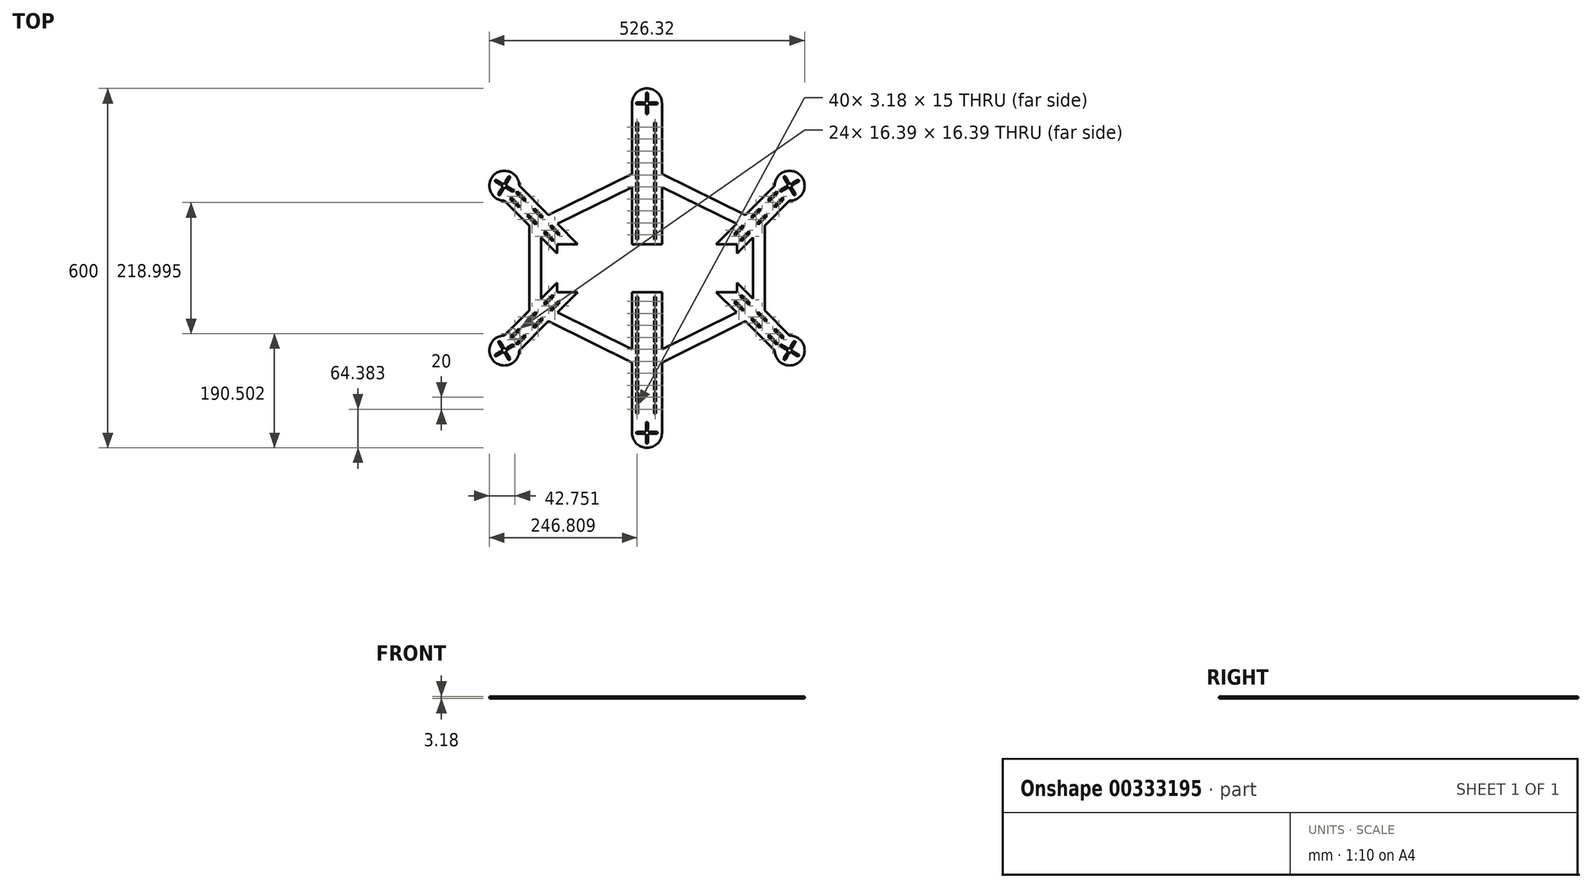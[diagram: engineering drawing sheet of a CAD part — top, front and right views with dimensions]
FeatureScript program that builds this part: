
annotation { "Feature Type Name" : "Feature", "Feature Type Description" : "" }
export const myFeature = defineFeature(function(context is Context, id is Id, definition is map)
    precondition{}
    {
        {
            var Q0;
            Q0=qCreatedBy(makeId("Top.planeOp"),FACE);
            var sketch = newSketch(context, id + "F0", { "sketchPlane" : qUnion([Q0])});
            skPoint(sketch, "E0.middle", {"position": v(0, 0) * mm});
            skCircle(sketch, "E1", {"center": v(0, 275) * mm, "radius": 25 * mm});
            skPoint(sketch, "E1.centerSnap0", {"position": v(0, 301.8) * mm});
            skCircle(sketch, "E2.1.0", {"center": v(-238.16, 137.5) * mm, "radius": 25 * mm});
            skLineSegment(sketch, "E3.bottom", {"start": v(150, -40) * mm, "end": v(-150, -40) * mm});
            skLineSegment(sketch, "E3.top", {"start": v(150, 40) * mm, "end": v(-150, 40) * mm});
            skLineSegment(sketch, "E3.left", {"start": v(150, -40) * mm, "end": v(150, 40) * mm});
            skLineSegment(sketch, "E3.right", {"start": v(-150, -40) * mm, "end": v(-150, 40) * mm});
            skLineSegment(sketch, "E4", {"start": v(-213.16, 137.5) * mm, "end": v(-115.66, 40) * mm});
            skLineSegment(sketch, "E5", {"start": v(-263.16, 137.5) * mm, "end": v(-150, 24.34) * mm});
            skCircle(sketch, "E6.MirrorC", {"center": v(-238.16, -137.5) * mm, "radius": 25 * mm});
            skLineSegment(sketch, "E7", {"start": v(0, 0) * mm, "end": v(0, 86.77) * mm, "construction": true});
            skLineSegment(sketch, "E8.MirrorCS", {"start": v(213.16, 137.5) * mm, "end": v(115.66, 40) * mm});
            skLineSegment(sketch, "E9.MirrorCS", {"start": v(263.16, 137.5) * mm, "end": v(150, 24.34) * mm});
            skCircle(sketch, "E10.MirrorC", {"center": v(238.16, 137.5) * mm, "radius": 25 * mm});
            skCircle(sketch, "E11.MirrorC", {"center": v(238.16, -137.5) * mm, "radius": 25 * mm});
            skLineSegment(sketch, "E12", {"start": v(0, 0) * mm, "end": v(-288.43, 0) * mm, "construction": true});
            skCircle(sketch, "E13.MirrorC", {"center": v(0, -275) * mm, "radius": 25 * mm});
            skLineSegment(sketch, "E14.bottom", {"start": v(-25, 275) * mm, "end": v(25, 275) * mm});
            skLineSegment(sketch, "E14.top", {"start": v(-25, 40) * mm, "end": v(25, 40) * mm});
            skLineSegment(sketch, "E14.left", {"start": v(-25, 275) * mm, "end": v(-25, 40) * mm});
            skLineSegment(sketch, "E14.right", {"start": v(25, 275) * mm, "end": v(25, 40) * mm});
            skLineSegment(sketch, "E15.MirrorCS", {"start": v(-25, -275) * mm, "end": v(-25, -40) * mm});
            skLineSegment(sketch, "E16.MirrorCS", {"start": v(25, -275) * mm, "end": v(25, -40) * mm});
            skLineSegment(sketch, "E17", {"start": v(-25, 157.5) * mm, "end": v(-25, 135.2) * mm});
            skLineSegment(sketch, "E18.MirrorCS", {"start": v(-213.16, -137.5) * mm, "end": v(-115.66, -40) * mm});
            skLineSegment(sketch, "E19.MirrorCS", {"start": v(-263.16, -137.5) * mm, "end": v(-150, -24.34) * mm});
            skLineSegment(sketch, "E20.MirrorCS", {"start": v(263.16, -137.5) * mm, "end": v(150, -24.34) * mm});
            skLineSegment(sketch, "E21.MirrorCS", {"start": v(213.16, -137.5) * mm, "end": v(115.66, -40) * mm});
            skLineSegment(sketch, "E22", {"start": v(-164.4, 88.75) * mm, "end": v(-25, 157.5) * mm});
            skLineSegment(sketch, "E23", {"start": v(-25, 135.2) * mm, "end": v(-149.47, 73.82) * mm});
            skLineSegment(sketch, "E24.MirrorCS", {"start": v(25, 135.2) * mm, "end": v(149.47, 73.82) * mm});
            skLineSegment(sketch, "E25.MirrorCS", {"start": v(164.4, 88.75) * mm, "end": v(25, 157.5) * mm});
            skLineSegment(sketch, "E26.MirrorCS", {"start": v(-25, -135.2) * mm, "end": v(-149.47, -73.82) * mm});
            skLineSegment(sketch, "E27.MirrorCS", {"start": v(-164.4, -88.75) * mm, "end": v(-25, -157.5) * mm});
            skLineSegment(sketch, "E28.MirrorCS", {"start": v(164.4, -88.75) * mm, "end": v(25, -157.5) * mm});
            skLineSegment(sketch, "E29.MirrorCS", {"start": v(25, -135.2) * mm, "end": v(149.47, -73.82) * mm});
            skLineSegment(sketch, "E30", {"start": v(-164.6, -38.94) * mm, "end": v(-188.74, -63.09) * mm});
            skLineSegment(sketch, "E31", {"start": v(-188.74, 63.09) * mm, "end": v(-164.6, 38.94) * mm});
            skLineSegment(sketch, "E32.MirrorCS", {"start": v(188.74, 63.09) * mm, "end": v(164.6, 38.94) * mm});
            skLineSegment(sketch, "E33", {"start": v(-176.67, 51.01) * mm, "end": v(-176.67, -51.01) * mm});
            skLineSegment(sketch, "E34", {"start": v(-196.67, 71.01) * mm, "end": v(-196.67, -71.01) * mm});
            skLineSegment(sketch, "E35.MirrorCS", {"start": v(176.67, 51.01) * mm, "end": v(176.67, -51.01) * mm});
            skLineSegment(sketch, "E36.MirrorCS", {"start": v(196.67, 71.01) * mm, "end": v(196.67, -71.01) * mm});
            skSolve(sketch);
        }
        {
            var Q0;
            Q0=qSketchRegion(id+"F0",true);
            var Q1;
            {var subQ2=sQuery(id+"F0.wireOp",EDGE,"E14.top");Q1=makeQuery(id+"F0.imprint","IMPRINT",FACE,{"disambiguationData":[TD([[makeQuery(id+"F0.imprint","IMPRINT",EDGE,{"derivedFrom":subQ2}),-1.0]])]});}
            extrude(context, id + "F1", {"entities" : qUnion([Q0, Q1]), "depth" : 3.17 * mm});
        }
        {
            var Q0;
            Q0=makeQuery(id+"F1.opExtrude","CAP_FACE",FACE,{"disambiguationData":[OSD([sQuery(id+"F0.wireOp",EDGE,"E1"),sQuery(id+"F0.wireOp",EDGE,"E2.1.0"),sQuery(id+"F0.wireOp",EDGE,"E3.bottom"),sQuery(id+"F0.wireOp",EDGE,"E3.top"),sQuery(id+"F0.wireOp",EDGE,"E3.left"),sQuery(id+"F0.wireOp",EDGE,"E3.right"),sQuery(id+"F0.wireOp",EDGE,"E4"),sQuery(id+"F0.wireOp",EDGE,"E5"),sQuery(id+"F0.wireOp",EDGE,"E6.MirrorC"),sQuery(id+"F0.wireOp",EDGE,"E8.MirrorCS"),sQuery(id+"F0.wireOp",EDGE,"E9.MirrorCS"),sQuery(id+"F0.wireOp",EDGE,"E10.MirrorC"),sQuery(id+"F0.wireOp",EDGE,"E11.MirrorC"),sQuery(id+"F0.wireOp",EDGE,"E13.MirrorC"),sQuery(id+"F0.wireOp",EDGE,"E14.left"),sQuery(id+"F0.wireOp",EDGE,"E14.right"),sQuery(id+"F0.wireOp",EDGE,"E15.MirrorCS"),sQuery(id+"F0.wireOp",EDGE,"E16.MirrorCS"),sQuery(id+"F0.wireOp",EDGE,"E18.MirrorCS"),sQuery(id+"F0.wireOp",EDGE,"E19.MirrorCS"),sQuery(id+"F0.wireOp",EDGE,"E21.MirrorCS"),sQuery(id+"F0.wireOp",EDGE,"E22"),sQuery(id+"F0.wireOp",EDGE,"E23"),sQuery(id+"F0.wireOp",EDGE,"E24.MirrorCS"),sQuery(id+"F0.wireOp",EDGE,"E25.MirrorCS"),sQuery(id+"F0.wireOp",EDGE,"E26.MirrorCS"),sQuery(id+"F0.wireOp",EDGE,"E27.MirrorCS"),sQuery(id+"F0.wireOp",EDGE,"E28.MirrorCS"),sQuery(id+"F0.wireOp",EDGE,"E29.MirrorCS"),sQuery(id+"F0.wireOp",EDGE,"E30"),sQuery(id+"F0.wireOp",EDGE,"E31"),sQuery(id+"F0.wireOp",EDGE,"E32.MirrorCS"),sQuery(id+"F0.wireOp",EDGE,"E20.MirrorCS"),sQuery(id+"F0.wireOp",EDGE,"E33"),sQuery(id+"F0.wireOp",EDGE,"E34"),sQuery(id+"F0.wireOp",EDGE,"E35.MirrorCS"),sQuery(id+"F0.wireOp",EDGE,"E36.MirrorCS")])],"isStart":false});
            var sketch = newSketch(context, id + "F2", { "sketchPlane" : qUnion([Q0])});
            skLineSegment(sketch, "E37.bottom", {"start": v(-17.94, 243.12) * mm, "end": v(-14.76, 243.12) * mm});
            skLineSegment(sketch, "E37.top", {"start": v(-17.94, 228.12) * mm, "end": v(-14.76, 228.12) * mm});
            skLineSegment(sketch, "E37.left", {"start": v(-17.94, 243.12) * mm, "end": v(-17.94, 228.12) * mm});
            skLineSegment(sketch, "E37.right", {"start": v(-14.76, 243.12) * mm, "end": v(-14.76, 228.12) * mm});
            skLineSegment(sketch, "E38.1.0.0", {"start": v(12.06, 243.12) * mm, "end": v(15.24, 243.12) * mm});
            skLineSegment(sketch, "E38.1.0.1", {"start": v(12.06, 243.12) * mm, "end": v(12.06, 228.12) * mm});
            skLineSegment(sketch, "E38.1.0.2", {"start": v(15.24, 243.12) * mm, "end": v(15.24, 228.12) * mm});
            skLineSegment(sketch, "E38.1.0.3", {"start": v(12.06, 228.12) * mm, "end": v(15.24, 228.12) * mm});
            skLineSegment(sketch, "E38.direction1", {"start": v(-17.94, 243.12) * mm, "end": v(12.06, 243.12) * mm, "construction": true});
            skLineSegment(sketch, "E39.0.1.0", {"start": v(-17.94, 223.12) * mm, "end": v(12.06, 223.12) * mm, "construction": true});
            skLineSegment(sketch, "E39.0.1.1", {"start": v(-14.76, 223.12) * mm, "end": v(-14.76, 208.12) * mm});
            skLineSegment(sketch, "E39.0.1.2", {"start": v(-17.94, 223.12) * mm, "end": v(-17.94, 208.12) * mm});
            skLineSegment(sketch, "E39.0.1.3", {"start": v(15.24, 223.12) * mm, "end": v(15.24, 208.12) * mm});
            skLineSegment(sketch, "E39.0.1.4", {"start": v(12.06, 223.12) * mm, "end": v(12.06, 208.12) * mm});
            skLineSegment(sketch, "E39.0.1.5", {"start": v(12.06, 208.12) * mm, "end": v(15.24, 208.12) * mm});
            skLineSegment(sketch, "E39.0.1.6", {"start": v(-17.94, 223.12) * mm, "end": v(-14.76, 223.12) * mm});
            skLineSegment(sketch, "E39.0.1.7", {"start": v(-17.94, 208.12) * mm, "end": v(-14.76, 208.12) * mm});
            skLineSegment(sketch, "E39.0.1.8", {"start": v(12.06, 223.12) * mm, "end": v(15.24, 223.12) * mm});
            skLineSegment(sketch, "E39.0.2.0", {"start": v(-17.94, 203.12) * mm, "end": v(12.06, 203.12) * mm, "construction": true});
            skLineSegment(sketch, "E39.0.2.1", {"start": v(-14.76, 203.12) * mm, "end": v(-14.76, 188.12) * mm});
            skLineSegment(sketch, "E39.0.2.2", {"start": v(-17.94, 203.12) * mm, "end": v(-17.94, 188.12) * mm});
            skLineSegment(sketch, "E39.0.2.3", {"start": v(15.24, 203.12) * mm, "end": v(15.24, 188.12) * mm});
            skLineSegment(sketch, "E39.0.2.4", {"start": v(12.06, 203.12) * mm, "end": v(12.06, 188.12) * mm});
            skLineSegment(sketch, "E39.0.2.5", {"start": v(12.06, 188.12) * mm, "end": v(15.24, 188.12) * mm});
            skLineSegment(sketch, "E39.0.2.6", {"start": v(-17.94, 203.12) * mm, "end": v(-14.76, 203.12) * mm});
            skLineSegment(sketch, "E39.0.2.7", {"start": v(-17.94, 188.12) * mm, "end": v(-14.76, 188.12) * mm});
            skLineSegment(sketch, "E39.0.2.8", {"start": v(12.06, 203.12) * mm, "end": v(15.24, 203.12) * mm});
            skLineSegment(sketch, "E39.0.3.0", {"start": v(-17.94, 183.12) * mm, "end": v(12.06, 183.12) * mm, "construction": true});
            skLineSegment(sketch, "E39.0.3.1", {"start": v(-14.76, 183.12) * mm, "end": v(-14.76, 168.12) * mm});
            skLineSegment(sketch, "E39.0.3.2", {"start": v(-17.94, 183.12) * mm, "end": v(-17.94, 168.12) * mm});
            skLineSegment(sketch, "E39.0.3.3", {"start": v(15.24, 183.12) * mm, "end": v(15.24, 168.12) * mm});
            skLineSegment(sketch, "E39.0.3.4", {"start": v(12.06, 183.12) * mm, "end": v(12.06, 168.12) * mm});
            skLineSegment(sketch, "E39.0.3.5", {"start": v(12.06, 168.12) * mm, "end": v(15.24, 168.12) * mm});
            skLineSegment(sketch, "E39.0.3.6", {"start": v(-17.94, 183.12) * mm, "end": v(-14.76, 183.12) * mm});
            skLineSegment(sketch, "E39.0.3.7", {"start": v(-17.94, 168.12) * mm, "end": v(-14.76, 168.12) * mm});
            skLineSegment(sketch, "E39.0.3.8", {"start": v(12.06, 183.12) * mm, "end": v(15.24, 183.12) * mm});
            skLineSegment(sketch, "E39.0.4.0", {"start": v(-17.94, 163.12) * mm, "end": v(12.06, 163.12) * mm, "construction": true});
            skLineSegment(sketch, "E39.0.4.1", {"start": v(-14.76, 163.12) * mm, "end": v(-14.76, 148.12) * mm});
            skLineSegment(sketch, "E39.0.4.2", {"start": v(-17.94, 163.12) * mm, "end": v(-17.94, 148.12) * mm});
            skLineSegment(sketch, "E39.0.4.3", {"start": v(15.24, 163.12) * mm, "end": v(15.24, 148.12) * mm});
            skLineSegment(sketch, "E39.0.4.4", {"start": v(12.06, 163.12) * mm, "end": v(12.06, 148.12) * mm});
            skLineSegment(sketch, "E39.0.4.5", {"start": v(12.06, 148.12) * mm, "end": v(15.24, 148.12) * mm});
            skLineSegment(sketch, "E39.0.4.6", {"start": v(-17.94, 163.12) * mm, "end": v(-14.76, 163.12) * mm});
            skLineSegment(sketch, "E39.0.4.7", {"start": v(-17.94, 148.12) * mm, "end": v(-14.76, 148.12) * mm});
            skLineSegment(sketch, "E39.0.4.8", {"start": v(12.06, 163.12) * mm, "end": v(15.24, 163.12) * mm});
            skLineSegment(sketch, "E39.0.5.0", {"start": v(-17.94, 143.12) * mm, "end": v(12.06, 143.12) * mm, "construction": true});
            skLineSegment(sketch, "E39.0.5.1", {"start": v(-14.76, 143.12) * mm, "end": v(-14.76, 128.12) * mm});
            skLineSegment(sketch, "E39.0.5.2", {"start": v(-17.94, 143.12) * mm, "end": v(-17.94, 128.12) * mm});
            skLineSegment(sketch, "E39.0.5.3", {"start": v(15.24, 143.12) * mm, "end": v(15.24, 128.12) * mm});
            skLineSegment(sketch, "E39.0.5.4", {"start": v(12.06, 143.12) * mm, "end": v(12.06, 128.12) * mm});
            skLineSegment(sketch, "E39.0.5.5", {"start": v(12.06, 128.12) * mm, "end": v(15.24, 128.12) * mm});
            skLineSegment(sketch, "E39.0.5.6", {"start": v(-17.94, 143.12) * mm, "end": v(-14.76, 143.12) * mm});
            skLineSegment(sketch, "E39.0.5.7", {"start": v(-17.94, 128.12) * mm, "end": v(-14.76, 128.12) * mm});
            skLineSegment(sketch, "E39.0.5.8", {"start": v(12.06, 143.12) * mm, "end": v(15.24, 143.12) * mm});
            skLineSegment(sketch, "E39.0.6.0", {"start": v(-17.94, 123.12) * mm, "end": v(12.06, 123.12) * mm, "construction": true});
            skLineSegment(sketch, "E39.0.6.1", {"start": v(-14.76, 123.12) * mm, "end": v(-14.76, 108.12) * mm});
            skLineSegment(sketch, "E39.0.6.2", {"start": v(-17.94, 123.12) * mm, "end": v(-17.94, 108.12) * mm});
            skLineSegment(sketch, "E39.0.6.3", {"start": v(15.24, 123.12) * mm, "end": v(15.24, 108.12) * mm});
            skLineSegment(sketch, "E39.0.6.4", {"start": v(12.06, 123.12) * mm, "end": v(12.06, 108.12) * mm});
            skLineSegment(sketch, "E39.0.6.5", {"start": v(12.06, 108.12) * mm, "end": v(15.24, 108.12) * mm});
            skLineSegment(sketch, "E39.0.6.6", {"start": v(-17.94, 123.12) * mm, "end": v(-14.76, 123.12) * mm});
            skLineSegment(sketch, "E39.0.6.7", {"start": v(-17.94, 108.12) * mm, "end": v(-14.76, 108.12) * mm});
            skLineSegment(sketch, "E39.0.6.8", {"start": v(12.06, 123.12) * mm, "end": v(15.24, 123.12) * mm});
            skLineSegment(sketch, "E39.0.7.0", {"start": v(-17.94, 103.12) * mm, "end": v(12.06, 103.12) * mm, "construction": true});
            skLineSegment(sketch, "E39.0.7.1", {"start": v(-14.76, 103.12) * mm, "end": v(-14.76, 88.12) * mm});
            skLineSegment(sketch, "E39.0.7.2", {"start": v(-17.94, 103.12) * mm, "end": v(-17.94, 88.12) * mm});
            skLineSegment(sketch, "E39.0.7.3", {"start": v(15.24, 103.12) * mm, "end": v(15.24, 88.12) * mm});
            skLineSegment(sketch, "E39.0.7.4", {"start": v(12.06, 103.12) * mm, "end": v(12.06, 88.12) * mm});
            skLineSegment(sketch, "E39.0.7.5", {"start": v(12.06, 88.12) * mm, "end": v(15.24, 88.12) * mm});
            skLineSegment(sketch, "E39.0.7.6", {"start": v(-17.94, 103.12) * mm, "end": v(-14.76, 103.12) * mm});
            skLineSegment(sketch, "E39.0.7.7", {"start": v(-17.94, 88.12) * mm, "end": v(-14.76, 88.12) * mm});
            skLineSegment(sketch, "E39.0.7.8", {"start": v(12.06, 103.12) * mm, "end": v(15.24, 103.12) * mm});
            skLineSegment(sketch, "E39.direction1", {"start": v(-17.94, 228.12) * mm, "end": v(7.06, 228.12) * mm, "construction": true});
            skLineSegment(sketch, "E39.direction2", {"start": v(-17.94, 228.12) * mm, "end": v(-17.94, 208.12) * mm, "construction": true});
            skLineSegment(sketch, "E40.MirrorCS", {"start": v(-17.94, -228.12) * mm, "end": v(-14.76, -228.12) * mm});
            skLineSegment(sketch, "E41.MirrorCS", {"start": v(-17.94, -223.12) * mm, "end": v(-14.76, -223.12) * mm});
            skLineSegment(sketch, "E42.MirrorCS", {"start": v(12.06, -223.12) * mm, "end": v(15.24, -223.12) * mm});
            skLineSegment(sketch, "E43.MirrorCS", {"start": v(-17.94, -208.12) * mm, "end": v(-14.76, -208.12) * mm});
            skLineSegment(sketch, "E44.MirrorCS", {"start": v(-17.94, -223.12) * mm, "end": v(-17.94, -208.12) * mm});
            skLineSegment(sketch, "E45.MirrorCS", {"start": v(12.06, -108.12) * mm, "end": v(15.24, -108.12) * mm});
            skLineSegment(sketch, "E46.MirrorCS", {"start": v(-17.94, -108.12) * mm, "end": v(-14.76, -108.12) * mm});
            skLineSegment(sketch, "E47.MirrorCS", {"start": v(12.06, -123.12) * mm, "end": v(15.24, -123.12) * mm});
            skLineSegment(sketch, "E48.MirrorCS", {"start": v(12.06, -228.12) * mm, "end": v(15.24, -228.12) * mm});
            skLineSegment(sketch, "E49.MirrorCS", {"start": v(-17.94, -183.12) * mm, "end": v(-14.76, -183.12) * mm});
            skLineSegment(sketch, "E50.MirrorCS", {"start": v(12.06, -103.12) * mm, "end": v(15.24, -103.12) * mm});
            skLineSegment(sketch, "E51.MirrorCS", {"start": v(-17.94, -148.12) * mm, "end": v(-14.76, -148.12) * mm});
            skLineSegment(sketch, "E52.MirrorCS", {"start": v(-17.94, -143.12) * mm, "end": v(-14.76, -143.12) * mm});
            skLineSegment(sketch, "E53.MirrorCS", {"start": v(-17.94, -103.12) * mm, "end": v(-14.76, -103.12) * mm});
            skLineSegment(sketch, "E54.MirrorCS", {"start": v(12.06, -183.12) * mm, "end": v(15.24, -183.12) * mm});
            skLineSegment(sketch, "E55.MirrorCS", {"start": v(12.06, -203.12) * mm, "end": v(15.24, -203.12) * mm});
            skLineSegment(sketch, "E56.MirrorCS", {"start": v(-17.94, -188.12) * mm, "end": v(-14.76, -188.12) * mm});
            skLineSegment(sketch, "E57.MirrorCS", {"start": v(-17.94, -228.12) * mm, "end": v(-17.94, -208.12) * mm, "construction": true});
            skLineSegment(sketch, "E58.MirrorCS", {"start": v(-14.76, -223.12) * mm, "end": v(-14.76, -208.12) * mm});
            skLineSegment(sketch, "E59.MirrorCS", {"start": v(12.06, -243.12) * mm, "end": v(12.06, -228.12) * mm});
            skLineSegment(sketch, "E60.MirrorCS", {"start": v(12.06, -243.12) * mm, "end": v(15.24, -243.12) * mm});
            skLineSegment(sketch, "E61.MirrorCS", {"start": v(-14.76, -243.12) * mm, "end": v(-14.76, -228.12) * mm});
            skLineSegment(sketch, "E62.MirrorCS", {"start": v(12.06, -223.12) * mm, "end": v(12.06, -208.12) * mm});
            skLineSegment(sketch, "E63.MirrorCS", {"start": v(-17.94, -203.12) * mm, "end": v(-14.76, -203.12) * mm});
            skLineSegment(sketch, "E64.MirrorCS", {"start": v(12.06, -143.12) * mm, "end": v(15.24, -143.12) * mm});
            skLineSegment(sketch, "E65.MirrorCS", {"start": v(-17.94, -123.12) * mm, "end": v(-14.76, -123.12) * mm});
            skLineSegment(sketch, "E66.MirrorCS", {"start": v(-17.94, -128.12) * mm, "end": v(-14.76, -128.12) * mm});
            skLineSegment(sketch, "E67.MirrorCS", {"start": v(12.06, -163.12) * mm, "end": v(15.24, -163.12) * mm});
            skLineSegment(sketch, "E68.MirrorCS", {"start": v(-17.94, -163.12) * mm, "end": v(-14.76, -163.12) * mm});
            skLineSegment(sketch, "E69.MirrorCS", {"start": v(15.24, -223.12) * mm, "end": v(15.24, -208.12) * mm});
            skLineSegment(sketch, "E70.MirrorCS", {"start": v(15.24, -243.12) * mm, "end": v(15.24, -228.12) * mm});
            skLineSegment(sketch, "E71.MirrorCS", {"start": v(-17.94, -243.12) * mm, "end": v(-17.94, -228.12) * mm});
            skLineSegment(sketch, "E72.MirrorCS", {"start": v(-17.94, -243.12) * mm, "end": v(-14.76, -243.12) * mm});
            skLineSegment(sketch, "E73.MirrorCS", {"start": v(12.06, -208.12) * mm, "end": v(15.24, -208.12) * mm});
            skLineSegment(sketch, "E74.MirrorCS", {"start": v(12.06, -188.12) * mm, "end": v(15.24, -188.12) * mm});
            skLineSegment(sketch, "E75.MirrorCS", {"start": v(15.24, -163.12) * mm, "end": v(15.24, -148.12) * mm});
            skLineSegment(sketch, "E76.MirrorCS", {"start": v(-14.76, -123.12) * mm, "end": v(-14.76, -108.12) * mm});
            skLineSegment(sketch, "E77.MirrorCS", {"start": v(12.06, -88.12) * mm, "end": v(15.24, -88.12) * mm});
            skLineSegment(sketch, "E78.MirrorCS", {"start": v(-14.76, -183.12) * mm, "end": v(-14.76, -168.12) * mm});
            skLineSegment(sketch, "E79.MirrorCS", {"start": v(-17.94, -203.12) * mm, "end": v(-17.94, -188.12) * mm});
            skLineSegment(sketch, "E80.MirrorCS", {"start": v(15.24, -203.12) * mm, "end": v(15.24, -188.12) * mm});
            skLineSegment(sketch, "E81.MirrorCS", {"start": v(12.06, -163.12) * mm, "end": v(12.06, -148.12) * mm});
            skLineSegment(sketch, "E82.MirrorCS", {"start": v(-17.94, -123.12) * mm, "end": v(-17.94, -108.12) * mm});
            skLineSegment(sketch, "E83.MirrorCS", {"start": v(15.24, -143.12) * mm, "end": v(15.24, -128.12) * mm});
            skLineSegment(sketch, "E84.MirrorCS", {"start": v(-14.76, -103.12) * mm, "end": v(-14.76, -88.12) * mm});
            skLineSegment(sketch, "E85.MirrorCS", {"start": v(-14.76, -163.12) * mm, "end": v(-14.76, -148.12) * mm});
            skLineSegment(sketch, "E86.MirrorCS", {"start": v(-17.94, -88.12) * mm, "end": v(-14.76, -88.12) * mm});
            skLineSegment(sketch, "E87.MirrorCS", {"start": v(12.06, -183.12) * mm, "end": v(12.06, -168.12) * mm});
            skLineSegment(sketch, "E88.MirrorCS", {"start": v(12.06, -123.12) * mm, "end": v(12.06, -108.12) * mm});
            skLineSegment(sketch, "E89.MirrorCS", {"start": v(-17.94, -168.12) * mm, "end": v(-14.76, -168.12) * mm});
            skLineSegment(sketch, "E90.MirrorCS", {"start": v(15.24, -123.12) * mm, "end": v(15.24, -108.12) * mm});
            skLineSegment(sketch, "E91.MirrorCS", {"start": v(12.06, -143.12) * mm, "end": v(12.06, -128.12) * mm});
            skLineSegment(sketch, "E92.MirrorCS", {"start": v(-17.94, -103.12) * mm, "end": v(-17.94, -88.12) * mm});
            skLineSegment(sketch, "E93.MirrorCS", {"start": v(12.06, -168.12) * mm, "end": v(15.24, -168.12) * mm});
            skLineSegment(sketch, "E94.MirrorCS", {"start": v(-17.94, -143.12) * mm, "end": v(-17.94, -128.12) * mm});
            skLineSegment(sketch, "E95.MirrorCS", {"start": v(12.06, -203.12) * mm, "end": v(12.06, -188.12) * mm});
            skLineSegment(sketch, "E96.MirrorCS", {"start": v(-17.94, -163.12) * mm, "end": v(-17.94, -148.12) * mm});
            skLineSegment(sketch, "E97.MirrorCS", {"start": v(-14.76, -143.12) * mm, "end": v(-14.76, -128.12) * mm});
            skLineSegment(sketch, "E98.MirrorCS", {"start": v(-17.94, -183.12) * mm, "end": v(-17.94, -168.12) * mm});
            skLineSegment(sketch, "E99.MirrorCS", {"start": v(15.24, -183.12) * mm, "end": v(15.24, -168.12) * mm});
            skLineSegment(sketch, "E100.MirrorCS", {"start": v(12.06, -103.12) * mm, "end": v(12.06, -88.12) * mm});
            skLineSegment(sketch, "E101.MirrorCS", {"start": v(-14.76, -203.12) * mm, "end": v(-14.76, -188.12) * mm});
            skLineSegment(sketch, "E102.MirrorCS", {"start": v(12.06, -128.12) * mm, "end": v(15.24, -128.12) * mm});
            skLineSegment(sketch, "E103.MirrorCS", {"start": v(15.24, -103.12) * mm, "end": v(15.24, -88.12) * mm});
            skLineSegment(sketch, "E104.MirrorCS", {"start": v(12.06, -148.12) * mm, "end": v(15.24, -148.12) * mm});
            skLineSegment(sketch, "E105.MirrorCS", {"start": v(-17.94, -223.12) * mm, "end": v(12.06, -223.12) * mm, "construction": true});
            skLineSegment(sketch, "E106.MirrorCS", {"start": v(-17.94, -228.12) * mm, "end": v(7.06, -228.12) * mm, "construction": true});
            skLineSegment(sketch, "E107.MirrorCS", {"start": v(-17.94, -143.12) * mm, "end": v(12.06, -143.12) * mm, "construction": true});
            skLineSegment(sketch, "E108.MirrorCS", {"start": v(-17.94, -243.12) * mm, "end": v(12.06, -243.12) * mm, "construction": true});
            skLineSegment(sketch, "E109.MirrorCS", {"start": v(-17.94, -163.12) * mm, "end": v(12.06, -163.12) * mm, "construction": true});
            skLineSegment(sketch, "E110.MirrorCS", {"start": v(-17.94, -123.12) * mm, "end": v(12.06, -123.12) * mm, "construction": true});
            skLineSegment(sketch, "E111.MirrorCS", {"start": v(-17.94, -103.12) * mm, "end": v(12.06, -103.12) * mm, "construction": true});
            skLineSegment(sketch, "E112.MirrorCS", {"start": v(-17.94, -183.12) * mm, "end": v(12.06, -183.12) * mm, "construction": true});
            skLineSegment(sketch, "E113.MirrorCS", {"start": v(-17.94, -203.12) * mm, "end": v(12.06, -203.12) * mm, "construction": true});
            skLineSegment(sketch, "E114.0.0.8", {"start": v(-17.94, 83.12) * mm, "end": v(12.06, 83.12) * mm, "construction": true});
            skLineSegment(sketch, "E114.3.0.8", {"start": v(-14.76, 83.12) * mm, "end": v(-14.76, 68.12) * mm});
            skLineSegment(sketch, "E114.6.0.8", {"start": v(-17.94, 83.12) * mm, "end": v(-17.94, 68.12) * mm});
            skLineSegment(sketch, "E114.9.0.8", {"start": v(15.24, 83.12) * mm, "end": v(15.24, 68.12) * mm});
            skLineSegment(sketch, "E114.12.0.8", {"start": v(12.06, 83.12) * mm, "end": v(12.06, 68.12) * mm});
            skLineSegment(sketch, "E114.15.0.8", {"start": v(12.06, 68.12) * mm, "end": v(15.24, 68.12) * mm});
            skLineSegment(sketch, "E114.18.0.8", {"start": v(-17.94, 83.12) * mm, "end": v(-14.76, 83.12) * mm});
            skLineSegment(sketch, "E114.21.0.8", {"start": v(-17.94, 68.12) * mm, "end": v(-14.76, 68.12) * mm});
            skLineSegment(sketch, "E114.24.0.8", {"start": v(12.06, 83.12) * mm, "end": v(15.24, 83.12) * mm});
            skLineSegment(sketch, "E114.0.0.9", {"start": v(-17.94, 63.12) * mm, "end": v(12.06, 63.12) * mm, "construction": true});
            skLineSegment(sketch, "E114.3.0.9", {"start": v(-14.76, 63.12) * mm, "end": v(-14.76, 48.12) * mm});
            skLineSegment(sketch, "E114.6.0.9", {"start": v(-17.94, 63.12) * mm, "end": v(-17.94, 48.12) * mm});
            skLineSegment(sketch, "E114.9.0.9", {"start": v(15.24, 63.12) * mm, "end": v(15.24, 48.12) * mm});
            skLineSegment(sketch, "E114.12.0.9", {"start": v(12.06, 63.12) * mm, "end": v(12.06, 48.12) * mm});
            skLineSegment(sketch, "E114.15.0.9", {"start": v(12.06, 48.12) * mm, "end": v(15.24, 48.12) * mm});
            skLineSegment(sketch, "E114.18.0.9", {"start": v(-17.94, 63.12) * mm, "end": v(-14.76, 63.12) * mm});
            skLineSegment(sketch, "E114.21.0.9", {"start": v(-17.94, 48.12) * mm, "end": v(-14.76, 48.12) * mm});
            skLineSegment(sketch, "E114.24.0.9", {"start": v(12.06, 63.12) * mm, "end": v(15.24, 63.12) * mm});
            skLineSegment(sketch, "E115.MirrorCS", {"start": v(12.06, -83.12) * mm, "end": v(15.24, -83.12) * mm});
            skLineSegment(sketch, "E116.MirrorCS", {"start": v(-17.94, -83.12) * mm, "end": v(-14.76, -83.12) * mm});
            skLineSegment(sketch, "E117.MirrorCS", {"start": v(12.06, -63.12) * mm, "end": v(15.24, -63.12) * mm});
            skLineSegment(sketch, "E118.MirrorCS", {"start": v(-17.94, -63.12) * mm, "end": v(-14.76, -63.12) * mm});
            skLineSegment(sketch, "E119.MirrorCS", {"start": v(-17.94, -68.12) * mm, "end": v(-14.76, -68.12) * mm});
            skLineSegment(sketch, "E120.MirrorCS", {"start": v(12.06, -68.12) * mm, "end": v(15.24, -68.12) * mm});
            skLineSegment(sketch, "E121.MirrorCS", {"start": v(-17.94, -48.12) * mm, "end": v(-14.76, -48.12) * mm});
            skLineSegment(sketch, "E122.MirrorCS", {"start": v(12.06, -48.12) * mm, "end": v(15.24, -48.12) * mm});
            skLineSegment(sketch, "E123.MirrorCS", {"start": v(12.06, -83.12) * mm, "end": v(12.06, -68.12) * mm});
            skLineSegment(sketch, "E124.MirrorCS", {"start": v(15.24, -83.12) * mm, "end": v(15.24, -68.12) * mm});
            skLineSegment(sketch, "E125.MirrorCS", {"start": v(-17.94, -83.12) * mm, "end": v(-17.94, -68.12) * mm});
            skLineSegment(sketch, "E126.MirrorCS", {"start": v(-14.76, -83.12) * mm, "end": v(-14.76, -68.12) * mm});
            skLineSegment(sketch, "E127.MirrorCS", {"start": v(-17.94, -63.12) * mm, "end": v(12.06, -63.12) * mm, "construction": true});
            skLineSegment(sketch, "E128.MirrorCS", {"start": v(-17.94, -83.12) * mm, "end": v(12.06, -83.12) * mm, "construction": true});
            skLineSegment(sketch, "E129.MirrorCS", {"start": v(12.06, -63.12) * mm, "end": v(12.06, -48.12) * mm});
            skLineSegment(sketch, "E130.MirrorCS", {"start": v(15.24, -63.12) * mm, "end": v(15.24, -48.12) * mm});
            skLineSegment(sketch, "E131.MirrorCS", {"start": v(-17.94, -63.12) * mm, "end": v(-17.94, -48.12) * mm});
            skLineSegment(sketch, "E132.MirrorCS", {"start": v(-14.76, -63.12) * mm, "end": v(-14.76, -48.12) * mm});
            skSolve(sketch);
        }
        {
            var Q0;
            Q0=qSketchRegion(id+"F2",true);
            extrude(context, id + "F3", {"entities" : qUnion([Q0]), "operationType" : NewBodyOperationType.REMOVE, "oppositeDirection" : true, "depth" : 25 * mm});
        }
        {
            var Q0;
            Q0=makeQuery(id+"F1.opExtrude","CAP_FACE",FACE,{"disambiguationData":[OSD([sQuery(id+"F0.wireOp",EDGE,"E1"),sQuery(id+"F0.wireOp",EDGE,"E2.1.0"),sQuery(id+"F0.wireOp",EDGE,"E3.bottom"),sQuery(id+"F0.wireOp",EDGE,"E3.top"),sQuery(id+"F0.wireOp",EDGE,"E3.left"),sQuery(id+"F0.wireOp",EDGE,"E3.right"),sQuery(id+"F0.wireOp",EDGE,"E4"),sQuery(id+"F0.wireOp",EDGE,"E5"),sQuery(id+"F0.wireOp",EDGE,"E6.MirrorC"),sQuery(id+"F0.wireOp",EDGE,"E8.MirrorCS"),sQuery(id+"F0.wireOp",EDGE,"E9.MirrorCS"),sQuery(id+"F0.wireOp",EDGE,"E10.MirrorC"),sQuery(id+"F0.wireOp",EDGE,"E11.MirrorC"),sQuery(id+"F0.wireOp",EDGE,"E13.MirrorC"),sQuery(id+"F0.wireOp",EDGE,"E14.left"),sQuery(id+"F0.wireOp",EDGE,"E14.right"),sQuery(id+"F0.wireOp",EDGE,"E15.MirrorCS"),sQuery(id+"F0.wireOp",EDGE,"E16.MirrorCS"),sQuery(id+"F0.wireOp",EDGE,"E18.MirrorCS"),sQuery(id+"F0.wireOp",EDGE,"E19.MirrorCS"),sQuery(id+"F0.wireOp",EDGE,"E21.MirrorCS"),sQuery(id+"F0.wireOp",EDGE,"E22"),sQuery(id+"F0.wireOp",EDGE,"E23"),sQuery(id+"F0.wireOp",EDGE,"E24.MirrorCS"),sQuery(id+"F0.wireOp",EDGE,"E25.MirrorCS"),sQuery(id+"F0.wireOp",EDGE,"E26.MirrorCS"),sQuery(id+"F0.wireOp",EDGE,"E27.MirrorCS"),sQuery(id+"F0.wireOp",EDGE,"E28.MirrorCS"),sQuery(id+"F0.wireOp",EDGE,"E29.MirrorCS"),sQuery(id+"F0.wireOp",EDGE,"E30"),sQuery(id+"F0.wireOp",EDGE,"E31"),sQuery(id+"F0.wireOp",EDGE,"E32.MirrorCS"),sQuery(id+"F0.wireOp",EDGE,"E20.MirrorCS"),sQuery(id+"F0.wireOp",EDGE,"E33"),sQuery(id+"F0.wireOp",EDGE,"E34"),sQuery(id+"F0.wireOp",EDGE,"E35.MirrorCS"),sQuery(id+"F0.wireOp",EDGE,"E36.MirrorCS")])],"isStart":false});
            var sketch = newSketch(context, id + "F4", { "sketchPlane" : qUnion([Q0])});
            skLineSegment(sketch, "E133.bottom", {"start": v(-201.96, 113.8) * mm, "end": v(-204.2, 111.56) * mm});
            skLineSegment(sketch, "E133.top", {"start": v(-216.1, 127.95) * mm, "end": v(-218.35, 125.7) * mm});
            skLineSegment(sketch, "E133.left", {"start": v(-201.96, 113.8) * mm, "end": v(-216.1, 127.95) * mm});
            skLineSegment(sketch, "E133.right", {"start": v(-204.2, 111.56) * mm, "end": v(-218.35, 125.7) * mm});
            skPoint(sketch, "E133.middle", {"position": v(-210.15, 119.75) * mm});
            skLineSegment(sketch, "E134.MirrorCS", {"start": v(-201.96, -113.8) * mm, "end": v(-204.2, -111.56) * mm});
            skLineSegment(sketch, "E135.MirrorCS", {"start": v(-216.1, -127.95) * mm, "end": v(-218.35, -125.7) * mm});
            skLineSegment(sketch, "E136.MirrorCS", {"start": v(-201.96, -113.8) * mm, "end": v(-216.1, -127.95) * mm});
            skLineSegment(sketch, "E137.MirrorCS", {"start": v(-204.2, -111.56) * mm, "end": v(-218.35, -125.7) * mm});
            skPoint(sketch, "E138.MirrorP", {"position": v(-210.15, -119.75) * mm});
            skPoint(sketch, "E139.1.0.0", {"position": v(-181.87, 91.47) * mm});
            skLineSegment(sketch, "E139.1.0.1", {"start": v(-173.68, 85.52) * mm, "end": v(-187.82, 99.66) * mm});
            skLineSegment(sketch, "E139.1.0.2", {"start": v(-175.92, 83.27) * mm, "end": v(-190.06, 97.42) * mm});
            skLineSegment(sketch, "E139.1.0.3", {"start": v(-173.68, 85.52) * mm, "end": v(-175.92, 83.27) * mm});
            skLineSegment(sketch, "E139.1.0.4", {"start": v(-187.82, 99.66) * mm, "end": v(-190.06, 97.42) * mm});
            skPoint(sketch, "E139.2.0.0", {"position": v(-153.59, 63.18) * mm});
            skLineSegment(sketch, "E139.2.0.1", {"start": v(-145.4, 57.24) * mm, "end": v(-159.53, 71.38) * mm});
            skLineSegment(sketch, "E139.2.0.2", {"start": v(-147.64, 55) * mm, "end": v(-161.78, 69.13) * mm});
            skLineSegment(sketch, "E139.2.0.3", {"start": v(-145.4, 57.24) * mm, "end": v(-147.64, 55) * mm});
            skLineSegment(sketch, "E139.2.0.4", {"start": v(-159.53, 71.38) * mm, "end": v(-161.78, 69.13) * mm});
            skLineSegment(sketch, "E139.direction1", {"start": v(-204.2, 111.56) * mm, "end": v(-175.92, 83.27) * mm, "construction": true});
            skLineSegment(sketch, "E140.MirrorCS", {"start": v(-173.68, -85.52) * mm, "end": v(-175.92, -83.27) * mm});
            skLineSegment(sketch, "E141.MirrorCS", {"start": v(-145.4, -57.24) * mm, "end": v(-147.64, -55) * mm});
            skLineSegment(sketch, "E142.MirrorCS", {"start": v(-187.82, -99.66) * mm, "end": v(-190.06, -97.42) * mm});
            skLineSegment(sketch, "E143.MirrorCS", {"start": v(-159.53, -71.38) * mm, "end": v(-161.78, -69.13) * mm});
            skLineSegment(sketch, "E144.MirrorCS", {"start": v(-145.4, -57.24) * mm, "end": v(-159.53, -71.38) * mm});
            skLineSegment(sketch, "E145.MirrorCS", {"start": v(-175.92, -83.27) * mm, "end": v(-190.06, -97.42) * mm});
            skLineSegment(sketch, "E146.MirrorCS", {"start": v(-173.68, -85.52) * mm, "end": v(-187.82, -99.66) * mm});
            skLineSegment(sketch, "E147.MirrorCS", {"start": v(-147.64, -55) * mm, "end": v(-161.78, -69.13) * mm});
            skPoint(sketch, "E148.MirrorP", {"position": v(-153.59, -63.18) * mm});
            skPoint(sketch, "E149.MirrorP", {"position": v(-181.87, -91.47) * mm});
            skLineSegment(sketch, "E150", {"start": v(-225.5, 124.84) * mm, "end": v(-150.52, 49.86) * mm, "construction": true});
            skLineSegment(sketch, "E151.MirrorCS", {"start": v(-214.46, 101.3) * mm, "end": v(-212.22, 103.55) * mm});
            skLineSegment(sketch, "E152.MirrorCS", {"start": v(-186.18, 73.02) * mm, "end": v(-183.93, 75.26) * mm});
            skLineSegment(sketch, "E153.MirrorCS", {"start": v(-228.6, 115.45) * mm, "end": v(-226.36, 117.7) * mm});
            skLineSegment(sketch, "E154.MirrorCS", {"start": v(-172.03, 58.88) * mm, "end": v(-169.79, 61.12) * mm});
            skLineSegment(sketch, "E155.MirrorCS", {"start": v(-157.9, 44.74) * mm, "end": v(-155.65, 46.98) * mm});
            skLineSegment(sketch, "E156.MirrorCS", {"start": v(-200.32, 87.16) * mm, "end": v(-198.07, 89.4) * mm});
            skLineSegment(sketch, "E157.MirrorCS", {"start": v(-183.93, 75.26) * mm, "end": v(-198.07, 89.4) * mm});
            skPoint(sketch, "E158.MirrorP", {"position": v(-220.4, 109.5) * mm});
            skLineSegment(sketch, "E159.MirrorCS", {"start": v(-212.22, 103.55) * mm, "end": v(-226.36, 117.7) * mm});
            skLineSegment(sketch, "E160.MirrorCS", {"start": v(-214.46, 101.3) * mm, "end": v(-228.6, 115.45) * mm});
            skLineSegment(sketch, "E161.MirrorCS", {"start": v(-212.22, 103.55) * mm, "end": v(-183.93, 75.26) * mm, "construction": true});
            skLineSegment(sketch, "E162.MirrorCS", {"start": v(-155.65, 46.98) * mm, "end": v(-169.79, 61.12) * mm});
            skLineSegment(sketch, "E163.MirrorCS", {"start": v(-157.9, 44.74) * mm, "end": v(-172.03, 58.88) * mm});
            skPoint(sketch, "E164.MirrorP", {"position": v(-163.84, 52.93) * mm});
            skPoint(sketch, "E165.MirrorP", {"position": v(-192.12, 81.21) * mm});
            skLineSegment(sketch, "E166.MirrorCS", {"start": v(-186.18, 73.02) * mm, "end": v(-200.32, 87.16) * mm});
            skLineSegment(sketch, "E167.MirrorCS", {"start": v(-186.18, -73.02) * mm, "end": v(-183.93, -75.26) * mm});
            skLineSegment(sketch, "E168.MirrorCS", {"start": v(-214.46, -101.3) * mm, "end": v(-212.22, -103.55) * mm});
            skLineSegment(sketch, "E169.MirrorCS", {"start": v(-228.6, -115.45) * mm, "end": v(-226.36, -117.7) * mm});
            skLineSegment(sketch, "E170.MirrorCS", {"start": v(-200.32, -87.16) * mm, "end": v(-198.07, -89.4) * mm});
            skLineSegment(sketch, "E171.MirrorCS", {"start": v(-172.03, -58.88) * mm, "end": v(-169.79, -61.12) * mm});
            skLineSegment(sketch, "E172.MirrorCS", {"start": v(-157.9, -44.74) * mm, "end": v(-155.65, -46.98) * mm});
            skLineSegment(sketch, "E173.MirrorCS", {"start": v(-183.93, -75.26) * mm, "end": v(-198.07, -89.4) * mm});
            skLineSegment(sketch, "E174.MirrorCS", {"start": v(-212.22, -103.55) * mm, "end": v(-226.36, -117.7) * mm});
            skLineSegment(sketch, "E175.MirrorCS", {"start": v(-155.65, -46.98) * mm, "end": v(-169.79, -61.12) * mm});
            skLineSegment(sketch, "E176.MirrorCS", {"start": v(-157.9, -44.74) * mm, "end": v(-172.03, -58.88) * mm});
            skLineSegment(sketch, "E177.MirrorCS", {"start": v(-186.18, -73.02) * mm, "end": v(-200.32, -87.16) * mm});
            skLineSegment(sketch, "E178.MirrorCS", {"start": v(-214.46, -101.3) * mm, "end": v(-228.6, -115.45) * mm});
            skPoint(sketch, "E179.MirrorP", {"position": v(-220.4, -109.5) * mm});
            skPoint(sketch, "E180.MirrorP", {"position": v(-163.84, -52.93) * mm});
            skPoint(sketch, "E181.MirrorP", {"position": v(-192.12, -81.21) * mm});
            skLineSegment(sketch, "E182.MirrorCS", {"start": v(-212.22, -103.55) * mm, "end": v(-183.93, -75.26) * mm, "construction": true});
            skLineSegment(sketch, "E183.MirrorCS", {"start": v(159.53, -71.38) * mm, "end": v(161.78, -69.13) * mm});
            skLineSegment(sketch, "E184.MirrorCS", {"start": v(173.68, -85.52) * mm, "end": v(175.92, -83.27) * mm});
            skLineSegment(sketch, "E185.MirrorCS", {"start": v(187.82, -99.66) * mm, "end": v(190.06, -97.42) * mm});
            skLineSegment(sketch, "E186.MirrorCS", {"start": v(214.46, 101.3) * mm, "end": v(212.22, 103.55) * mm});
            skLineSegment(sketch, "E187.MirrorCS", {"start": v(173.68, 85.52) * mm, "end": v(175.92, 83.27) * mm});
            skLineSegment(sketch, "E188.MirrorCS", {"start": v(145.4, -57.24) * mm, "end": v(147.64, -55) * mm});
            skLineSegment(sketch, "E189.MirrorCS", {"start": v(173.68, -85.52) * mm, "end": v(187.82, -99.66) * mm});
            skLineSegment(sketch, "E190.MirrorCS", {"start": v(145.4, -57.24) * mm, "end": v(159.53, -71.38) * mm});
            skLineSegment(sketch, "E191.MirrorCS", {"start": v(175.92, -83.27) * mm, "end": v(190.06, -97.42) * mm});
            skLineSegment(sketch, "E192.MirrorCS", {"start": v(147.64, -55) * mm, "end": v(161.78, -69.13) * mm});
            skLineSegment(sketch, "E193.MirrorCS", {"start": v(175.92, 83.27) * mm, "end": v(190.06, 97.42) * mm});
            skLineSegment(sketch, "E194.MirrorCS", {"start": v(216.1, 127.95) * mm, "end": v(218.35, 125.7) * mm});
            skLineSegment(sketch, "E195.MirrorCS", {"start": v(201.96, 113.8) * mm, "end": v(204.2, 111.56) * mm});
            skLineSegment(sketch, "E196.MirrorCS", {"start": v(159.53, 71.38) * mm, "end": v(161.78, 69.13) * mm});
            skLineSegment(sketch, "E197.MirrorCS", {"start": v(145.4, 57.24) * mm, "end": v(147.64, 55) * mm});
            skLineSegment(sketch, "E198.MirrorCS", {"start": v(187.82, 99.66) * mm, "end": v(190.06, 97.42) * mm});
            skLineSegment(sketch, "E199.MirrorCS", {"start": v(200.32, -87.16) * mm, "end": v(198.07, -89.4) * mm});
            skLineSegment(sketch, "E200.MirrorCS", {"start": v(173.68, 85.52) * mm, "end": v(187.82, 99.66) * mm});
            skLineSegment(sketch, "E201.MirrorCS", {"start": v(204.2, 111.56) * mm, "end": v(218.35, 125.7) * mm});
            skLineSegment(sketch, "E202.MirrorCS", {"start": v(201.96, 113.8) * mm, "end": v(216.1, 127.95) * mm});
            skLineSegment(sketch, "E203.MirrorCS", {"start": v(186.18, 73.02) * mm, "end": v(183.93, 75.26) * mm});
            skLineSegment(sketch, "E204.MirrorCS", {"start": v(172.03, -58.88) * mm, "end": v(169.79, -61.12) * mm});
            skLineSegment(sketch, "E205.MirrorCS", {"start": v(145.4, 57.24) * mm, "end": v(159.53, 71.38) * mm});
            skLineSegment(sketch, "E206.MirrorCS", {"start": v(228.6, 115.45) * mm, "end": v(226.36, 117.7) * mm});
            skLineSegment(sketch, "E207.MirrorCS", {"start": v(200.32, 87.16) * mm, "end": v(198.07, 89.4) * mm});
            skLineSegment(sketch, "E208.MirrorCS", {"start": v(172.03, 58.88) * mm, "end": v(169.79, 61.12) * mm});
            skLineSegment(sketch, "E209.MirrorCS", {"start": v(183.93, -75.26) * mm, "end": v(198.07, -89.4) * mm});
            skLineSegment(sketch, "E210.MirrorCS", {"start": v(183.93, 75.26) * mm, "end": v(198.07, 89.4) * mm});
            skLineSegment(sketch, "E211.MirrorCS", {"start": v(214.46, -101.3) * mm, "end": v(212.22, -103.55) * mm});
            skLineSegment(sketch, "E212.MirrorCS", {"start": v(204.2, 111.56) * mm, "end": v(175.92, 83.27) * mm, "construction": true});
            skLineSegment(sketch, "E213.MirrorCS", {"start": v(186.18, -73.02) * mm, "end": v(183.93, -75.26) * mm});
            skLineSegment(sketch, "E214.MirrorCS", {"start": v(204.2, -111.56) * mm, "end": v(218.35, -125.7) * mm});
            skLineSegment(sketch, "E215.MirrorCS", {"start": v(201.96, -113.8) * mm, "end": v(216.1, -127.95) * mm});
            skLineSegment(sketch, "E216.MirrorCS", {"start": v(214.46, -101.3) * mm, "end": v(228.6, -115.45) * mm});
            skLineSegment(sketch, "E217.MirrorCS", {"start": v(216.1, -127.95) * mm, "end": v(218.35, -125.7) * mm});
            skLineSegment(sketch, "E218.MirrorCS", {"start": v(201.96, -113.8) * mm, "end": v(204.2, -111.56) * mm});
            skLineSegment(sketch, "E219.MirrorCS", {"start": v(186.18, 73.02) * mm, "end": v(200.32, 87.16) * mm});
            skLineSegment(sketch, "E220.MirrorCS", {"start": v(155.65, 46.98) * mm, "end": v(169.79, 61.12) * mm});
            skLineSegment(sketch, "E221.MirrorCS", {"start": v(214.46, 101.3) * mm, "end": v(228.6, 115.45) * mm});
            skLineSegment(sketch, "E222.MirrorCS", {"start": v(212.22, 103.55) * mm, "end": v(226.36, 117.7) * mm});
            skLineSegment(sketch, "E223.MirrorCS", {"start": v(155.65, -46.98) * mm, "end": v(169.79, -61.12) * mm});
            skLineSegment(sketch, "E224.MirrorCS", {"start": v(157.9, -44.74) * mm, "end": v(155.65, -46.98) * mm});
            skLineSegment(sketch, "E225.MirrorCS", {"start": v(212.22, -103.55) * mm, "end": v(183.93, -75.26) * mm, "construction": true});
            skLineSegment(sketch, "E226.MirrorCS", {"start": v(212.22, 103.55) * mm, "end": v(183.93, 75.26) * mm, "construction": true});
            skLineSegment(sketch, "E227.MirrorCS", {"start": v(186.18, -73.02) * mm, "end": v(200.32, -87.16) * mm});
            skLineSegment(sketch, "E228.MirrorCS", {"start": v(228.6, -115.45) * mm, "end": v(226.36, -117.7) * mm});
            skLineSegment(sketch, "E229.MirrorCS", {"start": v(157.9, -44.74) * mm, "end": v(172.03, -58.88) * mm});
            skLineSegment(sketch, "E230.MirrorCS", {"start": v(157.9, 44.74) * mm, "end": v(172.03, 58.88) * mm});
            skLineSegment(sketch, "E231.MirrorCS", {"start": v(212.22, -103.55) * mm, "end": v(226.36, -117.7) * mm});
            skLineSegment(sketch, "E232.MirrorCS", {"start": v(157.9, 44.74) * mm, "end": v(155.65, 46.98) * mm});
            skLineSegment(sketch, "E233.MirrorCS", {"start": v(147.64, 55) * mm, "end": v(161.78, 69.13) * mm});
            skPoint(sketch, "E234.MirrorP", {"position": v(210.15, -119.75) * mm});
            skPoint(sketch, "E235.MirrorP", {"position": v(181.87, -91.47) * mm});
            skPoint(sketch, "E236.MirrorP", {"position": v(153.59, -63.18) * mm});
            skPoint(sketch, "E237.MirrorP", {"position": v(181.87, 91.47) * mm});
            skLineSegment(sketch, "E238.MirrorCS", {"start": v(225.5, 124.84) * mm, "end": v(150.52, 49.86) * mm, "construction": true});
            skPoint(sketch, "E239.MirrorP", {"position": v(163.84, 52.93) * mm});
            skPoint(sketch, "E240.MirrorP", {"position": v(220.4, -109.5) * mm});
            skPoint(sketch, "E241.MirrorP", {"position": v(192.12, 81.21) * mm});
            skPoint(sketch, "E242.MirrorP", {"position": v(163.84, -52.93) * mm});
            skPoint(sketch, "E243.MirrorP", {"position": v(153.59, 63.18) * mm});
            skPoint(sketch, "E244.MirrorP", {"position": v(220.4, 109.5) * mm});
            skPoint(sketch, "E245.MirrorP", {"position": v(192.12, -81.21) * mm});
            skPoint(sketch, "E246.MirrorP", {"position": v(210.15, 119.75) * mm});
            skSolve(sketch);
        }
        {
            var Q0;
            Q0=qSketchRegion(id+"F4",true);
            extrude(context, id + "F5", {"entities" : qUnion([Q0]), "operationType" : NewBodyOperationType.REMOVE, "oppositeDirection" : true, "depth" : 25 * mm});
        }
        {
            var Q0;
            Q0=qSketchRegion(id+"F2",true);
            extrude(context, id + "F6", {"entities" : qUnion([Q0]), "operationType" : NewBodyOperationType.REMOVE, "oppositeDirection" : true, "depth" : 3.17 * mm});
        }
        {
            var Q0;
            Q0=makeQuery(id+"F1.opExtrude","CAP_FACE",FACE,{"disambiguationData":[OSD([sQuery(id+"F0.wireOp",EDGE,"E1"),sQuery(id+"F0.wireOp",EDGE,"E2.1.0"),sQuery(id+"F0.wireOp",EDGE,"E3.bottom"),sQuery(id+"F0.wireOp",EDGE,"E3.top"),sQuery(id+"F0.wireOp",EDGE,"E3.left"),sQuery(id+"F0.wireOp",EDGE,"E3.right"),sQuery(id+"F0.wireOp",EDGE,"E4"),sQuery(id+"F0.wireOp",EDGE,"E5"),sQuery(id+"F0.wireOp",EDGE,"E6.MirrorC"),sQuery(id+"F0.wireOp",EDGE,"E8.MirrorCS"),sQuery(id+"F0.wireOp",EDGE,"E9.MirrorCS"),sQuery(id+"F0.wireOp",EDGE,"E10.MirrorC"),sQuery(id+"F0.wireOp",EDGE,"E11.MirrorC"),sQuery(id+"F0.wireOp",EDGE,"E13.MirrorC"),sQuery(id+"F0.wireOp",EDGE,"E14.left"),sQuery(id+"F0.wireOp",EDGE,"E14.right"),sQuery(id+"F0.wireOp",EDGE,"E15.MirrorCS"),sQuery(id+"F0.wireOp",EDGE,"E16.MirrorCS"),sQuery(id+"F0.wireOp",EDGE,"E18.MirrorCS"),sQuery(id+"F0.wireOp",EDGE,"E19.MirrorCS"),sQuery(id+"F0.wireOp",EDGE,"E21.MirrorCS"),sQuery(id+"F0.wireOp",EDGE,"E22"),sQuery(id+"F0.wireOp",EDGE,"E23"),sQuery(id+"F0.wireOp",EDGE,"E24.MirrorCS"),sQuery(id+"F0.wireOp",EDGE,"E25.MirrorCS"),sQuery(id+"F0.wireOp",EDGE,"E26.MirrorCS"),sQuery(id+"F0.wireOp",EDGE,"E27.MirrorCS"),sQuery(id+"F0.wireOp",EDGE,"E28.MirrorCS"),sQuery(id+"F0.wireOp",EDGE,"E29.MirrorCS"),sQuery(id+"F0.wireOp",EDGE,"E30"),sQuery(id+"F0.wireOp",EDGE,"E31"),sQuery(id+"F0.wireOp",EDGE,"E32.MirrorCS"),sQuery(id+"F0.wireOp",EDGE,"E20.MirrorCS"),sQuery(id+"F0.wireOp",EDGE,"E33"),sQuery(id+"F0.wireOp",EDGE,"E34"),sQuery(id+"F0.wireOp",EDGE,"E35.MirrorCS"),sQuery(id+"F0.wireOp",EDGE,"E36.MirrorCS")])],"isStart":false});
            var sketch = newSketch(context, id + "F7", { "sketchPlane" : qUnion([Q0])});
            skCircle(sketch, "E247", {"center": v(-22.77, 22.77) * mm, "radius": 1.5 * mm});
            skCircle(sketch, "E248.1.0", {"center": v(22.77, 22.77) * mm, "radius": 1.5 * mm});
            skCircle(sketch, "E248.2.0", {"center": v(22.77, -22.77) * mm, "radius": 1.5 * mm});
            skCircle(sketch, "E248.3.0", {"center": v(-22.77, -22.77) * mm, "radius": 1.5 * mm});
            skPoint(sketch, "E248.center", {"position": v(0, 0) * mm});
            skLineSegment(sketch, "E248.anchor1", {"start": v(0, 0) * mm, "end": v(-22.77, 22.77) * mm, "construction": true});
            skLineSegment(sketch, "E248.anchor2", {"start": v(0, 0) * mm, "end": v(-22.77, -22.77) * mm, "construction": true});
            skSolve(sketch);
        }
        {
            var Q0;
            Q0=qSketchRegion(id+"F7",true);
            extrude(context, id + "F8", {"entities" : qUnion([Q0]), "operationType" : NewBodyOperationType.REMOVE, "oppositeDirection" : true, "depth" : 25 * mm});
        }
        {
            var Q0;
            Q0=makeQuery(id+"F1.opExtrude","CAP_FACE",FACE,{"disambiguationData":[OSD([sQuery(id+"F0.wireOp",EDGE,"E1"),sQuery(id+"F0.wireOp",EDGE,"E2.1.0"),sQuery(id+"F0.wireOp",EDGE,"E3.bottom"),sQuery(id+"F0.wireOp",EDGE,"E3.top"),sQuery(id+"F0.wireOp",EDGE,"E3.left"),sQuery(id+"F0.wireOp",EDGE,"E3.right"),sQuery(id+"F0.wireOp",EDGE,"E4"),sQuery(id+"F0.wireOp",EDGE,"E5"),sQuery(id+"F0.wireOp",EDGE,"E6.MirrorC"),sQuery(id+"F0.wireOp",EDGE,"E8.MirrorCS"),sQuery(id+"F0.wireOp",EDGE,"E9.MirrorCS"),sQuery(id+"F0.wireOp",EDGE,"E10.MirrorC"),sQuery(id+"F0.wireOp",EDGE,"E11.MirrorC"),sQuery(id+"F0.wireOp",EDGE,"E13.MirrorC"),sQuery(id+"F0.wireOp",EDGE,"E14.left"),sQuery(id+"F0.wireOp",EDGE,"E14.right"),sQuery(id+"F0.wireOp",EDGE,"E15.MirrorCS"),sQuery(id+"F0.wireOp",EDGE,"E16.MirrorCS"),sQuery(id+"F0.wireOp",EDGE,"E18.MirrorCS"),sQuery(id+"F0.wireOp",EDGE,"E19.MirrorCS"),sQuery(id+"F0.wireOp",EDGE,"E21.MirrorCS"),sQuery(id+"F0.wireOp",EDGE,"E22"),sQuery(id+"F0.wireOp",EDGE,"E23"),sQuery(id+"F0.wireOp",EDGE,"E24.MirrorCS"),sQuery(id+"F0.wireOp",EDGE,"E25.MirrorCS"),sQuery(id+"F0.wireOp",EDGE,"E26.MirrorCS"),sQuery(id+"F0.wireOp",EDGE,"E27.MirrorCS"),sQuery(id+"F0.wireOp",EDGE,"E28.MirrorCS"),sQuery(id+"F0.wireOp",EDGE,"E29.MirrorCS"),sQuery(id+"F0.wireOp",EDGE,"E30"),sQuery(id+"F0.wireOp",EDGE,"E31"),sQuery(id+"F0.wireOp",EDGE,"E32.MirrorCS"),sQuery(id+"F0.wireOp",EDGE,"E20.MirrorCS"),sQuery(id+"F0.wireOp",EDGE,"E33"),sQuery(id+"F0.wireOp",EDGE,"E34"),sQuery(id+"F0.wireOp",EDGE,"E35.MirrorCS"),sQuery(id+"F0.wireOp",EDGE,"E36.MirrorCS")])],"isStart":false});
            var sketch = newSketch(context, id + "F9", { "sketchPlane" : qUnion([Q0])});
            skCircle(sketch, "E249", {"center": v(0, 275) * mm, "radius": 4 * mm});
            skLineSegment(sketch, "E250.bottom", {"start": v(1.5, 281.36) * mm, "end": v(-1.5, 281.36) * mm});
            skLineSegment(sketch, "E250.top", {"start": v(1.5, 291.36) * mm, "end": v(-1.5, 291.36) * mm});
            skLineSegment(sketch, "E250.left", {"start": v(1.5, 281.36) * mm, "end": v(1.5, 291.36) * mm});
            skLineSegment(sketch, "E250.right", {"start": v(-1.5, 281.36) * mm, "end": v(-1.5, 291.36) * mm});
            skPoint(sketch, "E250.middle", {"position": v(0, 286.36) * mm});
            skArc(sketch, "E251", {"start": v(-1.5, 281.36) * mm, "mid": v(0, 279.86) * mm, "end": v(1.5, 281.36) * mm});
            skArc(sketch, "E252", {"start": v(1.5, 291.36) * mm, "mid": v(0, 292.86) * mm, "end": v(-1.5, 291.36) * mm});
            skPoint(sketch, "E253.1.0", {"position": v(-11.36, 275) * mm});
            skLineSegment(sketch, "E253.1.1", {"start": v(-6.36, 276.5) * mm, "end": v(-6.36, 273.5) * mm});
            skLineSegment(sketch, "E253.1.2", {"start": v(-16.36, 276.5) * mm, "end": v(-16.36, 273.5) * mm});
            skLineSegment(sketch, "E253.1.3", {"start": v(-6.36, 276.5) * mm, "end": v(-16.36, 276.5) * mm});
            skLineSegment(sketch, "E253.1.4", {"start": v(-6.36, 273.5) * mm, "end": v(-16.36, 273.5) * mm});
            skArc(sketch, "E253.1.5", {"start": v(-6.36, 273.5) * mm, "mid": v(-4.86, 275) * mm, "end": v(-6.36, 276.5) * mm});
            skArc(sketch, "E253.1.6", {"start": v(-16.36, 276.5) * mm, "mid": v(-17.86, 275) * mm, "end": v(-16.36, 273.5) * mm});
            skPoint(sketch, "E253.2.0", {"position": v(0, 263.64) * mm});
            skLineSegment(sketch, "E253.2.1", {"start": v(-1.5, 268.64) * mm, "end": v(1.5, 268.64) * mm});
            skLineSegment(sketch, "E253.2.2", {"start": v(-1.5, 258.64) * mm, "end": v(1.5, 258.64) * mm});
            skLineSegment(sketch, "E253.2.3", {"start": v(-1.5, 268.64) * mm, "end": v(-1.5, 258.64) * mm});
            skLineSegment(sketch, "E253.2.4", {"start": v(1.5, 268.64) * mm, "end": v(1.5, 258.64) * mm});
            skArc(sketch, "E253.2.5", {"start": v(1.5, 268.64) * mm, "mid": v(0, 270.14) * mm, "end": v(-1.5, 268.64) * mm});
            skArc(sketch, "E253.2.6", {"start": v(-1.5, 258.64) * mm, "mid": v(0, 257.14) * mm, "end": v(1.5, 258.64) * mm});
            skPoint(sketch, "E253.3.0", {"position": v(11.36, 275) * mm});
            skLineSegment(sketch, "E253.3.1", {"start": v(6.36, 273.5) * mm, "end": v(6.36, 276.5) * mm});
            skLineSegment(sketch, "E253.3.2", {"start": v(16.36, 273.5) * mm, "end": v(16.36, 276.5) * mm});
            skLineSegment(sketch, "E253.3.3", {"start": v(6.36, 273.5) * mm, "end": v(16.36, 273.5) * mm});
            skLineSegment(sketch, "E253.3.4", {"start": v(6.36, 276.5) * mm, "end": v(16.36, 276.5) * mm});
            skArc(sketch, "E253.3.5", {"start": v(6.36, 276.5) * mm, "mid": v(4.86, 275) * mm, "end": v(6.36, 273.5) * mm});
            skArc(sketch, "E253.3.6", {"start": v(16.36, 273.5) * mm, "mid": v(17.86, 275) * mm, "end": v(16.36, 276.5) * mm});
            skLineSegment(sketch, "E254.1.0", {"start": v(-233.4, 133.02) * mm, "end": v(-224.73, 128.02) * mm});
            skArc(sketch, "E254.1.1", {"start": v(-228.67, 150.9) * mm, "mid": v(-229.22, 152.96) * mm, "end": v(-231.27, 152.4) * mm});
            skArc(sketch, "E254.1.2", {"start": v(-236.27, 143.75) * mm, "mid": v(-235.72, 141.7) * mm, "end": v(-233.67, 142.25) * mm});
            skLineSegment(sketch, "E254.1.3", {"start": v(-236.27, 143.75) * mm, "end": v(-231.27, 152.4) * mm});
            skPoint(sketch, "E254.1.4", {"position": v(-228.31, 131.82) * mm});
            skArc(sketch, "E254.1.5", {"start": v(-247.63, 124.08) * mm, "mid": v(-247.08, 122.03) * mm, "end": v(-245.03, 122.58) * mm});
            skArc(sketch, "E254.1.6", {"start": v(-240.03, 131.24) * mm, "mid": v(-240.58, 133.3) * mm, "end": v(-242.63, 132.74) * mm});
            skLineSegment(sketch, "E254.1.7", {"start": v(-240.03, 131.24) * mm, "end": v(-245.03, 122.58) * mm});
            skLineSegment(sketch, "E254.1.8", {"start": v(-242.63, 132.74) * mm, "end": v(-247.63, 124.08) * mm});
            skLineSegment(sketch, "E254.1.9", {"start": v(-233.67, 142.25) * mm, "end": v(-228.67, 150.9) * mm});
            skArc(sketch, "E254.1.10", {"start": v(-251.56, 146.97) * mm, "mid": v(-253.61, 146.42) * mm, "end": v(-253.06, 144.37) * mm});
            skArc(sketch, "E254.1.11", {"start": v(-244.4, 139.37) * mm, "mid": v(-242.35, 139.92) * mm, "end": v(-242.9, 141.97) * mm});
            skLineSegment(sketch, "E254.1.12", {"start": v(-244.4, 139.37) * mm, "end": v(-253.06, 144.37) * mm});
            skLineSegment(sketch, "E254.1.13", {"start": v(-242.9, 141.97) * mm, "end": v(-251.56, 146.97) * mm});
            skPoint(sketch, "E254.1.14", {"position": v(-243.83, 127.66) * mm});
            skCircle(sketch, "E254.1.15", {"center": v(-238.15, 137.5) * mm, "radius": 4 * mm});
            skPoint(sketch, "E254.1.16", {"position": v(-232.47, 147.33) * mm});
            skPoint(sketch, "E254.1.17", {"position": v(-238.15, 137.5) * mm});
            skLineSegment(sketch, "E254.1.18", {"start": v(-231.9, 135.62) * mm, "end": v(-223.23, 130.62) * mm});
            skArc(sketch, "E254.1.19", {"start": v(-231.9, 135.62) * mm, "mid": v(-233.94, 135.07) * mm, "end": v(-233.4, 133.02) * mm});
            skPoint(sketch, "E254.1.20", {"position": v(-247.98, 143.17) * mm});
            skArc(sketch, "E254.1.21", {"start": v(-224.73, 128.02) * mm, "mid": v(-222.69, 128.57) * mm, "end": v(-223.23, 130.62) * mm});
            skLineSegment(sketch, "E254.1.22", {"start": v(-224.73, 128.02) * mm, "end": v(-223.23, 130.62) * mm});
            skLineSegment(sketch, "E254.1.23", {"start": v(-247.63, 124.08) * mm, "end": v(-245.03, 122.58) * mm});
            skLineSegment(sketch, "E254.1.24", {"start": v(-242.63, 132.74) * mm, "end": v(-240.03, 131.24) * mm});
            skLineSegment(sketch, "E254.1.25", {"start": v(-233.4, 133.02) * mm, "end": v(-231.9, 135.62) * mm});
            skLineSegment(sketch, "E254.1.26", {"start": v(-228.67, 150.9) * mm, "end": v(-231.27, 152.4) * mm});
            skLineSegment(sketch, "E254.1.27", {"start": v(-251.56, 146.97) * mm, "end": v(-253.06, 144.37) * mm});
            skLineSegment(sketch, "E254.1.28", {"start": v(-242.9, 141.97) * mm, "end": v(-244.4, 139.37) * mm});
            skLineSegment(sketch, "E254.1.29", {"start": v(-233.67, 142.25) * mm, "end": v(-236.27, 143.75) * mm});
            skLineSegment(sketch, "E254.2.0", {"start": v(-231.89, -135.62) * mm, "end": v(-223.23, -130.62) * mm});
            skArc(sketch, "E254.2.1", {"start": v(-245.02, -122.59) * mm, "mid": v(-247.07, -122.04) * mm, "end": v(-247.62, -124.09) * mm});
            skArc(sketch, "E254.2.2", {"start": v(-242.62, -132.75) * mm, "mid": v(-240.57, -133.3) * mm, "end": v(-240.02, -131.25) * mm});
            skLineSegment(sketch, "E254.2.3", {"start": v(-242.62, -132.75) * mm, "end": v(-247.62, -124.09) * mm});
            skPoint(sketch, "E254.2.4", {"position": v(-228.3, -131.82) * mm});
            skArc(sketch, "E254.2.5", {"start": v(-231.26, -152.41) * mm, "mid": v(-229.21, -152.96) * mm, "end": v(-228.66, -150.91) * mm});
            skArc(sketch, "E254.2.6", {"start": v(-233.66, -142.25) * mm, "mid": v(-235.71, -141.7) * mm, "end": v(-236.26, -143.75) * mm});
            skLineSegment(sketch, "E254.2.7", {"start": v(-233.66, -142.25) * mm, "end": v(-228.66, -150.91) * mm});
            skLineSegment(sketch, "E254.2.8", {"start": v(-236.26, -143.75) * mm, "end": v(-231.26, -152.41) * mm});
            skLineSegment(sketch, "E254.2.9", {"start": v(-240.02, -131.25) * mm, "end": v(-245.02, -122.59) * mm});
            skArc(sketch, "E254.2.10", {"start": v(-253.06, -144.38) * mm, "mid": v(-253.6, -146.43) * mm, "end": v(-251.56, -146.98) * mm});
            skArc(sketch, "E254.2.11", {"start": v(-242.9, -141.98) * mm, "mid": v(-242.35, -139.93) * mm, "end": v(-244.4, -139.38) * mm});
            skLineSegment(sketch, "E254.2.12", {"start": v(-242.9, -141.98) * mm, "end": v(-251.56, -146.98) * mm});
            skLineSegment(sketch, "E254.2.13", {"start": v(-244.4, -139.38) * mm, "end": v(-253.06, -144.38) * mm});
            skPoint(sketch, "E254.2.14", {"position": v(-232.46, -147.33) * mm});
            skCircle(sketch, "E254.2.15", {"center": v(-238.14, -137.5) * mm, "radius": 4 * mm});
            skPoint(sketch, "E254.2.16", {"position": v(-243.82, -127.67) * mm});
            skPoint(sketch, "E254.2.17", {"position": v(-238.14, -137.5) * mm});
            skLineSegment(sketch, "E254.2.18", {"start": v(-233.39, -133.02) * mm, "end": v(-224.73, -128.02) * mm});
            skArc(sketch, "E254.2.19", {"start": v(-233.39, -133.02) * mm, "mid": v(-233.94, -135.07) * mm, "end": v(-231.89, -135.62) * mm});
            skPoint(sketch, "E254.2.20", {"position": v(-247.98, -143.18) * mm});
            skArc(sketch, "E254.2.21", {"start": v(-223.23, -130.62) * mm, "mid": v(-222.68, -128.57) * mm, "end": v(-224.73, -128.02) * mm});
            skLineSegment(sketch, "E254.2.22", {"start": v(-223.23, -130.62) * mm, "end": v(-224.73, -128.02) * mm});
            skLineSegment(sketch, "E254.2.23", {"start": v(-231.26, -152.41) * mm, "end": v(-228.66, -150.91) * mm});
            skLineSegment(sketch, "E254.2.24", {"start": v(-236.26, -143.75) * mm, "end": v(-233.66, -142.25) * mm});
            skLineSegment(sketch, "E254.2.25", {"start": v(-231.89, -135.62) * mm, "end": v(-233.39, -133.02) * mm});
            skLineSegment(sketch, "E254.2.26", {"start": v(-245.02, -122.59) * mm, "end": v(-247.62, -124.09) * mm});
            skLineSegment(sketch, "E254.2.27", {"start": v(-253.06, -144.38) * mm, "end": v(-251.56, -146.98) * mm});
            skLineSegment(sketch, "E254.2.28", {"start": v(-244.4, -139.38) * mm, "end": v(-242.9, -141.98) * mm});
            skLineSegment(sketch, "E254.2.29", {"start": v(-240.02, -131.25) * mm, "end": v(-242.62, -132.75) * mm});
            skLineSegment(sketch, "E254.3.0", {"start": v(1.52, -268.64) * mm, "end": v(1.52, -258.64) * mm});
            skArc(sketch, "E254.3.1", {"start": v(-16.34, -273.5) * mm, "mid": v(-17.84, -275) * mm, "end": v(-16.34, -276.5) * mm});
            skArc(sketch, "E254.3.2", {"start": v(-6.34, -276.5) * mm, "mid": v(-4.84, -275) * mm, "end": v(-6.34, -273.5) * mm});
            skLineSegment(sketch, "E254.3.3", {"start": v(-6.34, -276.5) * mm, "end": v(-16.34, -276.5) * mm});
            skPoint(sketch, "E254.3.4", {"position": v(0.02, -263.64) * mm});
            skArc(sketch, "E254.3.5", {"start": v(16.37, -276.5) * mm, "mid": v(17.87, -275) * mm, "end": v(16.37, -273.5) * mm});
            skArc(sketch, "E254.3.6", {"start": v(6.37, -273.5) * mm, "mid": v(4.87, -275) * mm, "end": v(6.37, -276.5) * mm});
            skLineSegment(sketch, "E254.3.7", {"start": v(6.37, -273.5) * mm, "end": v(16.37, -273.5) * mm});
            skLineSegment(sketch, "E254.3.8", {"start": v(6.37, -276.5) * mm, "end": v(16.37, -276.5) * mm});
            skLineSegment(sketch, "E254.3.9", {"start": v(-6.34, -273.5) * mm, "end": v(-16.34, -273.5) * mm});
            skArc(sketch, "E254.3.10", {"start": v(-1.48, -291.35) * mm, "mid": v(0.02, -292.85) * mm, "end": v(1.52, -291.35) * mm});
            skArc(sketch, "E254.3.11", {"start": v(1.52, -281.35) * mm, "mid": v(0.02, -279.85) * mm, "end": v(-1.48, -281.35) * mm});
            skLineSegment(sketch, "E254.3.12", {"start": v(1.52, -281.35) * mm, "end": v(1.52, -291.35) * mm});
            skLineSegment(sketch, "E254.3.13", {"start": v(-1.48, -281.35) * mm, "end": v(-1.48, -291.35) * mm});
            skPoint(sketch, "E254.3.14", {"position": v(11.37, -275) * mm});
            skCircle(sketch, "E254.3.15", {"center": v(0.02, -275) * mm, "radius": 4 * mm});
            skPoint(sketch, "E254.3.16", {"position": v(-11.34, -275) * mm});
            skPoint(sketch, "E254.3.17", {"position": v(0.02, -275) * mm});
            skLineSegment(sketch, "E254.3.18", {"start": v(-1.48, -268.64) * mm, "end": v(-1.48, -258.64) * mm});
            skArc(sketch, "E254.3.19", {"start": v(-1.48, -268.64) * mm, "mid": v(0.02, -270.14) * mm, "end": v(1.52, -268.64) * mm});
            skPoint(sketch, "E254.3.20", {"position": v(0.02, -286.35) * mm});
            skArc(sketch, "E254.3.21", {"start": v(1.52, -258.64) * mm, "mid": v(0.02, -257.14) * mm, "end": v(-1.48, -258.64) * mm});
            skLineSegment(sketch, "E254.3.22", {"start": v(1.52, -258.64) * mm, "end": v(-1.48, -258.64) * mm});
            skLineSegment(sketch, "E254.3.23", {"start": v(16.37, -276.5) * mm, "end": v(16.37, -273.5) * mm});
            skLineSegment(sketch, "E254.3.24", {"start": v(6.37, -276.5) * mm, "end": v(6.37, -273.5) * mm});
            skLineSegment(sketch, "E254.3.25", {"start": v(1.52, -268.64) * mm, "end": v(-1.48, -268.64) * mm});
            skLineSegment(sketch, "E254.3.26", {"start": v(-16.34, -273.5) * mm, "end": v(-16.34, -276.5) * mm});
            skLineSegment(sketch, "E254.3.27", {"start": v(-1.48, -291.35) * mm, "end": v(1.52, -291.35) * mm});
            skLineSegment(sketch, "E254.3.28", {"start": v(-1.48, -281.35) * mm, "end": v(1.52, -281.35) * mm});
            skLineSegment(sketch, "E254.3.29", {"start": v(-6.34, -273.5) * mm, "end": v(-6.34, -276.5) * mm});
            skLineSegment(sketch, "E254.4.0", {"start": v(233.41, -133) * mm, "end": v(224.75, -128) * mm});
            skArc(sketch, "E254.4.1", {"start": v(228.69, -150.9) * mm, "mid": v(229.24, -152.95) * mm, "end": v(231.29, -152.4) * mm});
            skArc(sketch, "E254.4.2", {"start": v(236.29, -143.74) * mm, "mid": v(235.74, -141.7) * mm, "end": v(233.69, -142.24) * mm});
            skLineSegment(sketch, "E254.4.3", {"start": v(236.29, -143.74) * mm, "end": v(231.29, -152.4) * mm});
            skPoint(sketch, "E254.4.4", {"position": v(228.33, -131.8) * mm});
            skArc(sketch, "E254.4.5", {"start": v(247.64, -124.07) * mm, "mid": v(247.1, -122.02) * mm, "end": v(245.04, -122.57) * mm});
            skArc(sketch, "E254.4.6", {"start": v(240.04, -131.23) * mm, "mid": v(240.6, -133.28) * mm, "end": v(242.64, -132.73) * mm});
            skLineSegment(sketch, "E254.4.7", {"start": v(240.04, -131.23) * mm, "end": v(245.04, -122.57) * mm});
            skLineSegment(sketch, "E254.4.8", {"start": v(242.64, -132.73) * mm, "end": v(247.64, -124.07) * mm});
            skLineSegment(sketch, "E254.4.9", {"start": v(233.69, -142.24) * mm, "end": v(228.69, -150.9) * mm});
            skArc(sketch, "E254.4.10", {"start": v(251.58, -146.96) * mm, "mid": v(253.63, -146.41) * mm, "end": v(253.08, -144.36) * mm});
            skArc(sketch, "E254.4.11", {"start": v(244.42, -139.36) * mm, "mid": v(242.37, -139.91) * mm, "end": v(242.92, -141.96) * mm});
            skLineSegment(sketch, "E254.4.12", {"start": v(244.42, -139.36) * mm, "end": v(253.08, -144.36) * mm});
            skLineSegment(sketch, "E254.4.13", {"start": v(242.92, -141.96) * mm, "end": v(251.58, -146.96) * mm});
            skPoint(sketch, "E254.4.14", {"position": v(243.84, -127.65) * mm});
            skCircle(sketch, "E254.4.15", {"center": v(238.17, -137.49) * mm, "radius": 4 * mm});
            skPoint(sketch, "E254.4.16", {"position": v(232.49, -147.32) * mm});
            skPoint(sketch, "E254.4.17", {"position": v(238.17, -137.49) * mm});
            skLineSegment(sketch, "E254.4.18", {"start": v(231.91, -135.6) * mm, "end": v(223.25, -130.6) * mm});
            skArc(sketch, "E254.4.19", {"start": v(231.91, -135.6) * mm, "mid": v(233.96, -135.06) * mm, "end": v(233.41, -133) * mm});
            skPoint(sketch, "E254.4.20", {"position": v(248, -143.16) * mm});
            skArc(sketch, "E254.4.21", {"start": v(224.75, -128) * mm, "mid": v(222.7, -128.56) * mm, "end": v(223.25, -130.6) * mm});
            skLineSegment(sketch, "E254.4.22", {"start": v(224.75, -128) * mm, "end": v(223.25, -130.6) * mm});
            skLineSegment(sketch, "E254.4.23", {"start": v(247.64, -124.07) * mm, "end": v(245.04, -122.57) * mm});
            skLineSegment(sketch, "E254.4.24", {"start": v(242.64, -132.73) * mm, "end": v(240.04, -131.23) * mm});
            skLineSegment(sketch, "E254.4.25", {"start": v(233.41, -133) * mm, "end": v(231.91, -135.6) * mm});
            skLineSegment(sketch, "E254.4.26", {"start": v(228.69, -150.9) * mm, "end": v(231.29, -152.4) * mm});
            skLineSegment(sketch, "E254.4.27", {"start": v(251.58, -146.96) * mm, "end": v(253.08, -144.36) * mm});
            skLineSegment(sketch, "E254.4.28", {"start": v(242.92, -141.96) * mm, "end": v(244.42, -139.36) * mm});
            skLineSegment(sketch, "E254.4.29", {"start": v(233.69, -142.24) * mm, "end": v(236.29, -143.74) * mm});
            skLineSegment(sketch, "E254.5.0", {"start": v(231.9, 135.63) * mm, "end": v(223.24, 130.63) * mm});
            skArc(sketch, "E254.5.1", {"start": v(245.04, 122.6) * mm, "mid": v(247.08, 122.05) * mm, "end": v(247.63, 124.1) * mm});
            skArc(sketch, "E254.5.2", {"start": v(242.63, 132.76) * mm, "mid": v(240.58, 133.3) * mm, "end": v(240.04, 131.26) * mm});
            skLineSegment(sketch, "E254.5.3", {"start": v(242.63, 132.76) * mm, "end": v(247.63, 124.1) * mm});
            skPoint(sketch, "E254.5.4", {"position": v(228.32, 131.83) * mm});
            skArc(sketch, "E254.5.5", {"start": v(231.28, 152.42) * mm, "mid": v(229.23, 152.97) * mm, "end": v(228.68, 150.92) * mm});
            skArc(sketch, "E254.5.6", {"start": v(233.68, 142.26) * mm, "mid": v(235.73, 141.71) * mm, "end": v(236.28, 143.76) * mm});
            skLineSegment(sketch, "E254.5.7", {"start": v(233.68, 142.26) * mm, "end": v(228.68, 150.92) * mm});
            skLineSegment(sketch, "E254.5.8", {"start": v(236.28, 143.76) * mm, "end": v(231.28, 152.42) * mm});
            skLineSegment(sketch, "E254.5.9", {"start": v(240.04, 131.26) * mm, "end": v(245.04, 122.6) * mm});
            skArc(sketch, "E254.5.10", {"start": v(253.07, 144.39) * mm, "mid": v(253.62, 146.44) * mm, "end": v(251.57, 146.99) * mm});
            skArc(sketch, "E254.5.11", {"start": v(242.91, 141.99) * mm, "mid": v(242.36, 139.94) * mm, "end": v(244.41, 139.39) * mm});
            skLineSegment(sketch, "E254.5.12", {"start": v(242.91, 141.99) * mm, "end": v(251.57, 146.99) * mm});
            skLineSegment(sketch, "E254.5.13", {"start": v(244.41, 139.39) * mm, "end": v(253.07, 144.39) * mm});
            skPoint(sketch, "E254.5.14", {"position": v(232.48, 147.34) * mm});
            skCircle(sketch, "E254.5.15", {"center": v(238.16, 137.5) * mm, "radius": 4 * mm});
            skPoint(sketch, "E254.5.16", {"position": v(243.83, 127.68) * mm});
            skPoint(sketch, "E254.5.17", {"position": v(238.16, 137.5) * mm});
            skLineSegment(sketch, "E254.5.18", {"start": v(233.4, 133.03) * mm, "end": v(224.74, 128.03) * mm});
            skArc(sketch, "E254.5.19", {"start": v(233.4, 133.03) * mm, "mid": v(233.95, 135.08) * mm, "end": v(231.9, 135.63) * mm});
            skPoint(sketch, "E254.5.20", {"position": v(248, 143.19) * mm});
            skArc(sketch, "E254.5.21", {"start": v(223.24, 130.63) * mm, "mid": v(222.7, 128.58) * mm, "end": v(224.74, 128.03) * mm});
            skLineSegment(sketch, "E254.5.22", {"start": v(223.24, 130.63) * mm, "end": v(224.74, 128.03) * mm});
            skLineSegment(sketch, "E254.5.23", {"start": v(231.28, 152.42) * mm, "end": v(228.68, 150.92) * mm});
            skLineSegment(sketch, "E254.5.24", {"start": v(236.28, 143.76) * mm, "end": v(233.68, 142.26) * mm});
            skLineSegment(sketch, "E254.5.25", {"start": v(231.9, 135.63) * mm, "end": v(233.4, 133.03) * mm});
            skLineSegment(sketch, "E254.5.26", {"start": v(245.04, 122.6) * mm, "end": v(247.63, 124.1) * mm});
            skLineSegment(sketch, "E254.5.27", {"start": v(253.07, 144.39) * mm, "end": v(251.57, 146.99) * mm});
            skLineSegment(sketch, "E254.5.28", {"start": v(244.41, 139.39) * mm, "end": v(242.91, 141.99) * mm});
            skLineSegment(sketch, "E254.5.29", {"start": v(240.04, 131.26) * mm, "end": v(242.63, 132.76) * mm});
            skPoint(sketch, "E254.center", {"position": v(0, 0) * mm});
            skSolve(sketch);
        }
        {
            var Q0;
            Q0=qSketchRegion(id+"F9",true);
            extrude(context, id + "F10", {"entities" : qUnion([Q0]), "operationType" : NewBodyOperationType.REMOVE, "oppositeDirection" : true, "depth" : 25 * mm});
        }
    });
